# Revit family: NAXOS-Table
name_source: partatom
category: Lighting Fixtures
units: mm (PartAtom-declared; Revit-internal decimal feet)

## family parameters
Always vertical = Yes
Cut with Voids When Loaded = No
Light Source = No
OmniClass Number = 23.80.70.00
OmniClass Title = Lighting
Part Type = Normal
Room Calculation Point = No
Round Connector Dimension = Use Diameter
Shared = No
Work Plane-Based = Yes

## types (4) — shared parameters
Country = Europe
Default Elevation = 1219 mm
Description = TABLE LAMP
Designer = Studio Debonademeo
Diameter Bulb = 15 mm  [stored 0.0492126 ft]
Manufacturer = Vistosi
Manufacturer country = Italy
Model = NAXOS
Type Comments = Studio Debonademeo
URL = https://vistosi.com
URL Product Page = https://vistosi.it
zero-valued in all types: Depth

## per-type parameters (varying)
| type | A | NAXOS_Base | NAXOS_Lampshade | Width |
| NAXOS_LT 50 | 185 mm | NAXOS_Base : NAXOS LT 50 | NAXOS_Lampshade : NAXOS_LT 50 | 45 mm |
| NAXOS LT MN | 100 mm  [stored 0.328084 ft] | NAXOS_Base : NAXOS LT MN | NAXOS_Lampshade : NAXOS_LT MN | 16 mm |
| NAXOS LT 33 | 135 mm  [stored 0.442913 ft] | NAXOS_Base : NAXOS LT 33 | NAXOS_Lampshade : NAXOS_LT 33 | 20 mm |
| NAXOS LT 76 | 315 mm | NAXOS_Base : NAXOS LT 76 | NAXOS_Lampshade : NAXOS_LT 76 | 48 mm |

note: [stored X ft] marks values corroborated as IEEE doubles in the binary element streams (Revit-internal decimal feet)

## geometry (parser evidence)
native form markers: Sweep x7
no freeform markers — native parametric forms only
